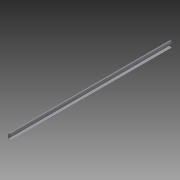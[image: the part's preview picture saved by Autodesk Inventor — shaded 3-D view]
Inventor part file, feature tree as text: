
AUTODESK INVENTOR PART (.ipt)
format: ipt  version: 2015 SP1 (Build 190203100, 203)  size: 110,592 bytes
history: native  units: in
note: dims shown in document units (in); Inventor stores cm internally (conversion verified against a paired STEP export)
features: extrude x1, sketch x1
ambient origin geometry x8: Origin, YZ Plane, XZ Plane, XY Plane, X Axis, Y Axis, Z Axis, Center Point
bodies: Solid1 (feature_tree)
feature tree (2):
  extrude  "Extrusion1"  Depth=60.0in
  sketch  "Sketch1"  dims[d0=0.5in d1=2.0in d2=0.5in d3=180.0deg d4=2.0in d5=90.0deg d6=0.5in d7=0.5in d8=0.25in d9=0.25in d10=0.25in d11=150.0deg d12=0.25in d13=30.0deg d14=0.0625in d15=90.0deg d16=1.0625in d17=0.25in d18=60.0deg d19=120.0deg d20=90.0deg d21=0.0625in d22=0.25in d23=0.25in d24=0.0625in d25=0.3125in d26=0.0in d27=60.0in d28=0.0in]
